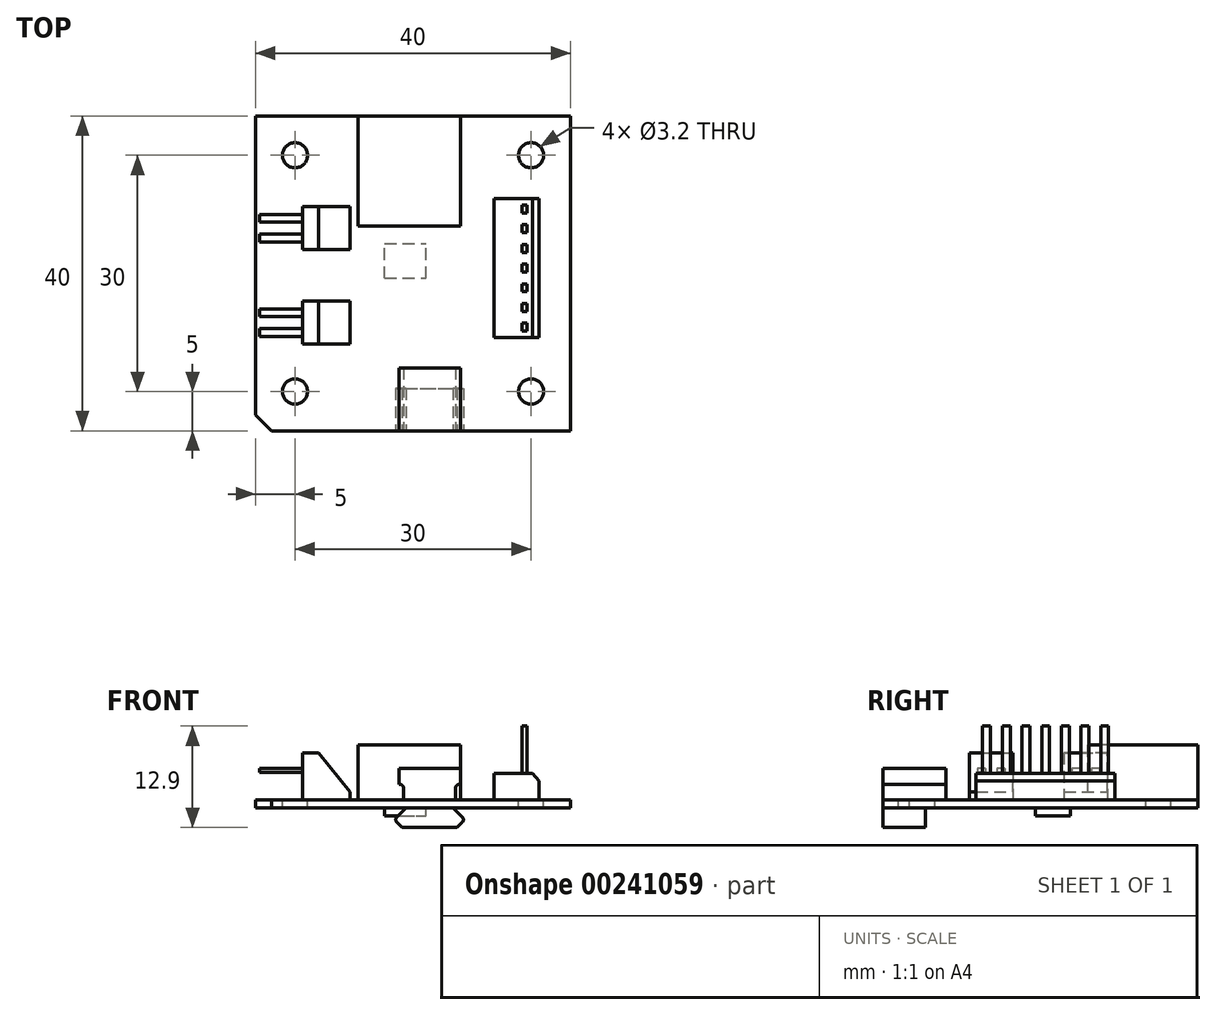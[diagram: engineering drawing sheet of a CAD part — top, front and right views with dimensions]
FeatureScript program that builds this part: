
annotation { "Feature Type Name" : "Feature", "Feature Type Description" : "" }
export const myFeature = defineFeature(function(context is Context, id is Id, definition is map)
    precondition{}
    {
        {
            var Q0;
            Q0=qCreatedBy(makeId("Top.planeOp"),FACE);
            var sketch = newSketch(context, id + "F0", { "sketchPlane" : qUnion([Q0])});
            skLineSegment(sketch, "E0", {"start": v(-20, 20) * mm, "end": v(-20, -18) * mm});
            skLineSegment(sketch, "E1", {"start": v(-18, -20) * mm, "end": v(20, -20) * mm});
            skLineSegment(sketch, "E2", {"start": v(-20, -18) * mm, "end": v(-18, -20) * mm});
            skLineSegment(sketch, "E3", {"start": v(20, 20) * mm, "end": v(20, -20) * mm});
            skLineSegment(sketch, "E4", {"start": v(-20, 20) * mm, "end": v(20, 20) * mm});
            skPoint(sketch, "E5", {"position": v(0, 20) * mm});
            skPoint(sketch, "E6.positionSnap0", {"position": v(20, 0) * mm});
            skSolve(sketch);
        }
        {
            var Q0;
            Q0=makeQuery(id+"F0.imprint","IMPRINT",FACE,{"disambiguationData":[TD([[makeQuery(id+"F0.imprint","IMPRINT",EDGE,{"derivedFrom":sQuery(id+"F0.wireOp",EDGE,"E0")}),1.0]])]});
            extrude(context, id + "F1", {"entities" : qUnion([Q0]), "oppositeDirection" : true, "depth" : 1 * mm});
        }
        {
            var Q0;
            Q0=makeQuery(id+"F1.opExtrude","CAP_FACE",FACE,{"disambiguationData":[OSD([sQuery(id+"F0.wireOp",EDGE,"E0"),sQuery(id+"F0.wireOp",EDGE,"E1"),sQuery(id+"F0.wireOp",EDGE,"wq8KnrCC-K7iv-RLEB-TxgK-UJwxQWP4eZSJ"),sQuery(id+"F0.wireOp",EDGE,"KpYQeONx-miEN-Xjcd-WnpJ-AOX53lkAbQX0"),sQuery(id+"F0.wireOp",EDGE,"kbl2VPpv-Qmzk-IL6K-4Z6z-1lDPvhAcDkAd")])],"isStart":true});
            var sketch = newSketch(context, id + "F2", { "sketchPlane" : qUnion([Q0])});
            skCircle(sketch, "E7", {"center": v(-15, 15) * mm, "radius": 1.6 * mm});
            skCircle(sketch, "E8", {"center": v(-15, -15) * mm, "radius": 1.6 * mm});
            skCircle(sketch, "E9", {"center": v(15, -15) * mm, "radius": 1.6 * mm});
            skCircle(sketch, "E10", {"center": v(15, 15) * mm, "radius": 1.6 * mm});
            skLineSegment(sketch, "E11", {"start": v(-15, 15) * mm, "end": v(15, 15) * mm, "construction": true});
            skLineSegment(sketch, "E12", {"start": v(-15, 15) * mm, "end": v(-15, -15) * mm, "construction": true});
            skPoint(sketch, "E13", {"position": v(0, 15) * mm});
            skPoint(sketch, "E14", {"position": v(-15, 0) * mm});
            skSolve(sketch);
        }
        {
            var Q0;
            Q0 = qSketchRegion(id + "F2", true);
            var Q1;
            Q1=makeQuery(id+"F1.opExtrude","CAP_FACE",FACE,{"disambiguationData":[OSD([sQuery(id+"F0.wireOp",EDGE,"E0"),sQuery(id+"F0.wireOp",EDGE,"E1"),sQuery(id+"F0.wireOp",EDGE,"wq8KnrCC-K7iv-RLEB-TxgK-UJwxQWP4eZSJ"),sQuery(id+"F0.wireOp",EDGE,"KpYQeONx-miEN-Xjcd-WnpJ-AOX53lkAbQX0"),sQuery(id+"F0.wireOp",EDGE,"kbl2VPpv-Qmzk-IL6K-4Z6z-1lDPvhAcDkAd")])],"isStart":false});
            extrude(context, id + "F3", {"entities" : qUnion([Q0]), "operationType" : NewBodyOperationType.REMOVE, "endBound" : BoundingType.UP_TO_SURFACE, "oppositeDirection" : true, "endBoundEntityFace" : qUnion([Q1]), "depth" : 25 * mm});
        }
        {
            var Q0;
            Q0=makeQuery(id+"F1.opExtrude","CAP_FACE",FACE,{"disambiguationData":[OSD([sQuery(id+"F0.wireOp",EDGE,"E0"),sQuery(id+"F0.wireOp",EDGE,"E1"),sQuery(id+"F0.wireOp",EDGE,"wq8KnrCC-K7iv-RLEB-TxgK-UJwxQWP4eZSJ"),sQuery(id+"F0.wireOp",EDGE,"KpYQeONx-miEN-Xjcd-WnpJ-AOX53lkAbQX0"),sQuery(id+"F0.wireOp",EDGE,"kbl2VPpv-Qmzk-IL6K-4Z6z-1lDPvhAcDkAd")])],"isStart":true});
            var sketch = newSketch(context, id + "F4", { "sketchPlane" : qUnion([Q0])});
            skLineSegment(sketch, "E15.bottom", {"start": v(-7, 20) * mm, "end": v(6, 20) * mm});
            skLineSegment(sketch, "E15.top", {"start": v(-7, 6) * mm, "end": v(6, 6) * mm});
            skLineSegment(sketch, "E15.left", {"start": v(-7, 20) * mm, "end": v(-7, 6) * mm});
            skLineSegment(sketch, "E15.right", {"start": v(6, 20) * mm, "end": v(6, 6) * mm});
            skLineSegment(sketch, "E16.0.0", {"start": v(20, -20) * mm, "end": v(20, 20) * mm});
            skLineSegment(sketch, "E16.0.1", {"start": v(20, 20) * mm, "end": v(-20, 20) * mm});
            skLineSegment(sketch, "E16.0.2", {"start": v(-20, 20) * mm, "end": v(-20, -18) * mm});
            skLineSegment(sketch, "E16.0.3", {"start": v(-20, -18) * mm, "end": v(-18, -20) * mm});
            skLineSegment(sketch, "E16.0.4", {"start": v(-18, -20) * mm, "end": v(20, -20) * mm});
            skSolve(sketch);
        }
        {
            var Q0;
            Q0=makeQuery(id+"F4.imprint","IMPRINT",FACE,{"disambiguationData":[TD([[makeQuery(id+"F4.imprint","IMPRINT",EDGE,{"derivedFrom":sQuery(id+"F4.wireOp",EDGE,"E15.top")}),1.0]])]});
            extrude(context, id + "F5", {"entities" : qUnion([Q0]), "depth" : 7 * mm});
        }
        {
            var Q0;
            Q0=makeQuery(id+"F1.opExtrude","SWEPT_FACE",FACE,{"disambiguationData":[OSD([sQuery(id+"F0.wireOp",EDGE,"E1")])]});
            var sketch = newSketch(context, id + "F6", { "sketchPlane" : qUnion([Q0])});
            skLineSegment(sketch, "E17.0.0", {"start": v(-18, 0) * mm, "end": v(-18, 0) * mm});
            skLineSegment(sketch, "E17.0.1", {"start": v(-18, 0) * mm, "end": v(-18, -1) * mm});
            skLineSegment(sketch, "E17.0.2", {"start": v(-18, -1) * mm, "end": v(-18, -1) * mm});
            skLineSegment(sketch, "E17.0.3", {"start": v(-18, 0) * mm, "end": v(-18, -1) * mm});
            skLineSegment(sketch, "E18", {"start": v(-1.2, 0) * mm, "end": v(-1.2, 2) * mm});
            skLineSegment(sketch, "E19", {"start": v(-1.2, 2) * mm, "end": v(-1.8, 2) * mm});
            skLineSegment(sketch, "E20", {"start": v(-1.8, 2) * mm, "end": v(-1.8, 4) * mm});
            skLineSegment(sketch, "E21", {"start": v(-1.8, 4) * mm, "end": v(6, 4) * mm});
            skLineSegment(sketch, "E22", {"start": v(6, 4) * mm, "end": v(6, 2) * mm});
            skLineSegment(sketch, "E23", {"start": v(6, 2) * mm, "end": v(5.4, 2) * mm});
            skLineSegment(sketch, "E24", {"start": v(5.4, 2) * mm, "end": v(5.4, 0) * mm});
            skLineSegment(sketch, "E25", {"start": v(5.4, 0) * mm, "end": v(-1.2, 0) * mm});
            skLineSegment(sketch, "E26.0.0", {"start": v(-7, 0) * mm, "end": v(6, 0) * mm});
            skLineSegment(sketch, "E26.0.1", {"start": v(6, 0) * mm, "end": v(6, 7) * mm});
            skLineSegment(sketch, "E26.0.2", {"start": v(6, 7) * mm, "end": v(-7, 7) * mm});
            skLineSegment(sketch, "E26.0.3", {"start": v(-7, 7) * mm, "end": v(-7, 0) * mm});
            skSolve(sketch);
        }
        {
            var Q0;
            {var subQ1=sQuery(id+"F6.wireOp",EDGE,"E18");Q0=makeQuery(id+"F6.imprint","IMPRINT",FACE,{"disambiguationData":[TD([[makeQuery(id+"F6.imprint","IMPRINT",EDGE,{"derivedFrom":subQ1}),-1.0]])]});}
            extrude(context, id + "F7", {"entities" : qUnion([Q0]), "oppositeDirection" : true, "depth" : 8 * mm});
        }
        {
            var Q0;
            Q0=makeQuery(id+"F7.opExtrude","SWEPT_EDGE",EDGE,{"disambiguationData":[OSD([sQuery(id+"F6.wireOp",EDGE,"E18"),sQuery(id+"F6.wireOp",EDGE,"E19")])]});
            var Q1;
            Q1=makeQuery(id+"F7.opExtrude","SWEPT_EDGE",EDGE,{"disambiguationData":[OSD([sQuery(id+"F6.wireOp",EDGE,"E23"),sQuery(id+"F6.wireOp",EDGE,"E24")])]});
            fillet(context, id + "F8", {"entities" : qUnion([Q0, Q1]), "radius" : 0.5 * mm, "tangentPropagation" : true, "allowEdgeOverflow" : false});
        }
        {
            var Q0;
            Q0=makeQuery(id+"F1.opExtrude","SWEPT_FACE",FACE,{"disambiguationData":[OSD([sQuery(id+"F0.wireOp",EDGE,"E1")])]});
            var sketch = newSketch(context, id + "F9", { "sketchPlane" : qUnion([Q0])});
            skLineSegment(sketch, "E27.0.0", {"start": v(-18, 0) * mm, "end": v(-18, 0) * mm});
            skLineSegment(sketch, "E27.0.1", {"start": v(-18, 0) * mm, "end": v(-18, -1) * mm});
            skLineSegment(sketch, "E27.0.2", {"start": v(-18, -1) * mm, "end": v(-18, -1) * mm});
            skLineSegment(sketch, "E27.0.3", {"start": v(-18, 0) * mm, "end": v(-18, -1) * mm});
            skLineSegment(sketch, "E28.0.0", {"start": v(5.9, 2) * mm, "end": v(6, 2) * mm});
            skLineSegment(sketch, "E28.0.1", {"start": v(6, 2) * mm, "end": v(6, 4) * mm});
            skLineSegment(sketch, "E28.0.2", {"start": v(6, 4) * mm, "end": v(-1.8, 4) * mm});
            skLineSegment(sketch, "E28.0.3", {"start": v(-1.8, 4) * mm, "end": v(-1.8, 2) * mm});
            skLineSegment(sketch, "E28.0.4", {"start": v(-1.8, 2) * mm, "end": v(-1.7, 2) * mm});
            skArc(sketch, "E28.0.5", {"start": v(-1.7, 2) * mm, "mid": v(-1.35, 1.85) * mm, "end": v(-1.2, 1.5) * mm});
            skLineSegment(sketch, "E28.0.6", {"start": v(-1.2, 1.5) * mm, "end": v(-1.2, 0) * mm});
            skLineSegment(sketch, "E28.0.7", {"start": v(-1.2, 0) * mm, "end": v(5.4, 0) * mm});
            skLineSegment(sketch, "E28.0.8", {"start": v(5.4, 0) * mm, "end": v(5.4, 1.5) * mm});
            skArc(sketch, "E28.0.9", {"start": v(5.4, 1.5) * mm, "mid": v(5.55, 1.85) * mm, "end": v(5.9, 2) * mm});
            skLineSegment(sketch, "E29", {"start": v(-0.9, -1) * mm, "end": v(-2.05, -2.15) * mm});
            skLineSegment(sketch, "E30", {"start": v(-2.05, -2.85) * mm, "end": v(-1.4, -3.5) * mm});
            skLineSegment(sketch, "E31", {"start": v(-1.4, -3.5) * mm, "end": v(5.6, -3.5) * mm});
            skLineSegment(sketch, "E32", {"start": v(5.6, -3.5) * mm, "end": v(6.25, -2.85) * mm});
            skLineSegment(sketch, "E33", {"start": v(6.25, -2.15) * mm, "end": v(5.1, -1) * mm});
            skLineSegment(sketch, "E34", {"start": v(5.1, -1) * mm, "end": v(-0.9, -1) * mm});
            skPoint(sketch, "E35", {"position": v(2.1, 4) * mm});
            skPoint(sketch, "E36", {"position": v(2.1, -1) * mm});
            skPoint(sketch, "E37", {"position": v(2.1, -3.5) * mm});
            skPoint(sketch, "E38.visualSharp", {"position": v(-2.4, -2.5) * mm});
            skArc(sketch, "E38.filletArc", {"start": v(-2.05, -2.15) * mm, "mid": v(-2.2, -2.5) * mm, "end": v(-2.05, -2.85) * mm});
            skPoint(sketch, "E39.visualSharp", {"position": v(6.6, -2.5) * mm});
            skArc(sketch, "E39.filletArc", {"start": v(6.25, -2.85) * mm, "mid": v(6.4, -2.5) * mm, "end": v(6.25, -2.15) * mm});
            skSolve(sketch);
        }
        {
            var Q0;
            Q0=makeQuery(id+"F9.imprint","IMPRINT",FACE,{"disambiguationData":[TD([[makeQuery(id+"F9.imprint","IMPRINT",EDGE,{"derivedFrom":sQuery(id+"F9.wireOp",EDGE,"E29")}),1.0]])]});
            extrude(context, id + "F10", {"entities" : qUnion([Q0]), "oppositeDirection" : true, "depth" : 5.4 * mm});
        }
        {
            var Q0;
            Q0=makeQuery(id+"F1.opExtrude","CAP_FACE",FACE,{"disambiguationData":[OSD([sQuery(id+"F0.wireOp",EDGE,"E0"),sQuery(id+"F0.wireOp",EDGE,"E1"),sQuery(id+"F0.wireOp",EDGE,"E2"),sQuery(id+"F0.wireOp",EDGE,"E3"),sQuery(id+"F0.wireOp",EDGE,"E4")])],"isStart":false});
            var sketch = newSketch(context, id + "F11", { "sketchPlane" : qUnion([Q0])});
            skLineSegment(sketch, "E40.bottom", {"start": v(-3.6, 0.6) * mm, "end": v(1.65, 0.6) * mm});
            skLineSegment(sketch, "E40.top", {"start": v(-3.6, -3.8) * mm, "end": v(1.65, -3.8) * mm});
            skLineSegment(sketch, "E40.left", {"start": v(-3.6, 0.6) * mm, "end": v(-3.6, -3.8) * mm});
            skLineSegment(sketch, "E40.right", {"start": v(1.65, 0.6) * mm, "end": v(1.65, -3.8) * mm});
            skSolve(sketch);
        }
        {
            var Q0;
            Q0=makeQuery(id+"F11.imprint","IMPRINT",FACE,{"disambiguationData":[TD([[makeQuery(id+"F11.imprint","IMPRINT",EDGE,{"derivedFrom":sQuery(id+"F11.wireOp",EDGE,"E40.bottom")}),-1.0]])]});
            extrude(context, id + "F12", {"entities" : qUnion([Q0]), "depth" : 1 * mm});
        }
        {
            var Q0;
            Q0=makeQuery(id+"F1.opExtrude","CAP_FACE",FACE,{"disambiguationData":[OSD([sQuery(id+"F0.wireOp",EDGE,"E0"),sQuery(id+"F0.wireOp",EDGE,"E1"),sQuery(id+"F0.wireOp",EDGE,"E2"),sQuery(id+"F0.wireOp",EDGE,"E3"),sQuery(id+"F0.wireOp",EDGE,"E4")])],"isStart":true});
            var sketch = newSketch(context, id + "F13", { "sketchPlane" : qUnion([Q0])});
            skLineSegment(sketch, "E41.bottom", {"start": v(10.3, 9.5) * mm, "end": v(16, 9.5) * mm});
            skLineSegment(sketch, "E41.top", {"start": v(10.3, -8.15) * mm, "end": v(16, -8.15) * mm});
            skLineSegment(sketch, "E41.left", {"start": v(10.3, 9.5) * mm, "end": v(10.3, -8.15) * mm});
            skLineSegment(sketch, "E41.right", {"start": v(16, 9.5) * mm, "end": v(16, -8.15) * mm});
            skSolve(sketch);
        }
        {
            var Q0;
            Q0=makeQuery(id+"F13.imprint","IMPRINT",FACE,{"disambiguationData":[TD([[makeQuery(id+"F13.imprint","IMPRINT",EDGE,{"derivedFrom":sQuery(id+"F13.wireOp",EDGE,"E41.bottom")}),-1.0]])]});
            extrude(context, id + "F14", {"entities" : qUnion([Q0]), "depth" : 3.4 * mm});
        }
        {
            var Q0;
            Q0=makeQuery(id+"F14.opExtrude","CAP_FACE",FACE,{"disambiguationData":[OSD([sQuery(id+"F13.wireOp",EDGE,"E41.bottom"),sQuery(id+"F13.wireOp",EDGE,"E41.top"),sQuery(id+"F13.wireOp",EDGE,"E41.left"),sQuery(id+"F13.wireOp",EDGE,"E41.right")])],"isStart":false});
            var sketch = newSketch(context, id + "F15", { "sketchPlane" : qUnion([Q0])});
            skLineSegment(sketch, "E42.bottom", {"start": v(13.85, 8.67) * mm, "end": v(14.5, 8.67) * mm});
            skLineSegment(sketch, "E42.top", {"start": v(13.85, 7.67) * mm, "end": v(14.5, 7.67) * mm});
            skLineSegment(sketch, "E42.left", {"start": v(13.85, 8.67) * mm, "end": v(13.85, 7.67) * mm});
            skLineSegment(sketch, "E42.right", {"start": v(14.5, 8.67) * mm, "end": v(14.5, 7.67) * mm});
            skLineSegment(sketch, "E43.bottom", {"start": v(13.85, 6.17) * mm, "end": v(14.5, 6.17) * mm});
            skLineSegment(sketch, "E43.top", {"start": v(13.85, 5.17) * mm, "end": v(14.5, 5.17) * mm});
            skLineSegment(sketch, "E43.left", {"start": v(13.85, 6.17) * mm, "end": v(13.85, 5.17) * mm});
            skLineSegment(sketch, "E43.right", {"start": v(14.5, 6.17) * mm, "end": v(14.5, 5.17) * mm});
            skLineSegment(sketch, "E44.bottom", {"start": v(13.85, 3.67) * mm, "end": v(14.5, 3.67) * mm});
            skLineSegment(sketch, "E44.top", {"start": v(13.85, 2.67) * mm, "end": v(14.5, 2.67) * mm});
            skLineSegment(sketch, "E44.left", {"start": v(13.85, 3.67) * mm, "end": v(13.85, 2.67) * mm});
            skLineSegment(sketch, "E44.right", {"start": v(14.5, 3.67) * mm, "end": v(14.5, 2.67) * mm});
            skLineSegment(sketch, "E45.bottom", {"start": v(13.85, 1.17) * mm, "end": v(14.5, 1.17) * mm});
            skLineSegment(sketch, "E45.top", {"start": v(13.85, 0.17) * mm, "end": v(14.5, 0.17) * mm});
            skLineSegment(sketch, "E45.left", {"start": v(13.85, 1.17) * mm, "end": v(13.85, 0.17) * mm});
            skLineSegment(sketch, "E45.right", {"start": v(14.5, 1.17) * mm, "end": v(14.5, 0.17) * mm});
            skLineSegment(sketch, "E46.bottom", {"start": v(14.5, -1.33) * mm, "end": v(13.85, -1.33) * mm});
            skLineSegment(sketch, "E46.top", {"start": v(14.5, -2.33) * mm, "end": v(13.85, -2.33) * mm});
            skLineSegment(sketch, "E46.left", {"start": v(14.5, -1.33) * mm, "end": v(14.5, -2.33) * mm});
            skLineSegment(sketch, "E46.right", {"start": v(13.85, -1.33) * mm, "end": v(13.85, -2.33) * mm});
            skLineSegment(sketch, "E47.bottom", {"start": v(14.5, -3.83) * mm, "end": v(13.85, -3.83) * mm});
            skLineSegment(sketch, "E47.top", {"start": v(14.5, -4.83) * mm, "end": v(13.85, -4.83) * mm});
            skLineSegment(sketch, "E47.left", {"start": v(14.5, -3.83) * mm, "end": v(14.5, -4.83) * mm});
            skLineSegment(sketch, "E47.right", {"start": v(13.85, -3.83) * mm, "end": v(13.85, -4.83) * mm});
            skLineSegment(sketch, "E48.bottom", {"start": v(14.5, -6.33) * mm, "end": v(13.85, -6.33) * mm});
            skLineSegment(sketch, "E48.top", {"start": v(14.5, -7.33) * mm, "end": v(13.85, -7.33) * mm});
            skLineSegment(sketch, "E48.left", {"start": v(14.5, -6.33) * mm, "end": v(14.5, -7.33) * mm});
            skLineSegment(sketch, "E48.right", {"start": v(13.85, -6.33) * mm, "end": v(13.85, -7.33) * mm});
            skLineSegment(sketch, "E49", {"start": v(14.5, 8.67) * mm, "end": v(14.5, 6.17) * mm, "construction": true});
            skLineSegment(sketch, "E50", {"start": v(14.5, 6.17) * mm, "end": v(14.5, 3.67) * mm, "construction": true});
            skLineSegment(sketch, "E51", {"start": v(14.5, 3.67) * mm, "end": v(14.5, 1.17) * mm, "construction": true});
            skLineSegment(sketch, "E52", {"start": v(14.5, 1.17) * mm, "end": v(14.5, -1.33) * mm, "construction": true});
            skLineSegment(sketch, "E53", {"start": v(14.5, -1.33) * mm, "end": v(14.5, -3.83) * mm, "construction": true});
            skLineSegment(sketch, "E54", {"start": v(14.5, -3.83) * mm, "end": v(14.5, -6.33) * mm, "construction": true});
            skLineSegment(sketch, "E55", {"start": v(13.85, 8.67) * mm, "end": v(13.85, -7.33) * mm, "construction": true});
            skPoint(sketch, "E56", {"position": v(13.85, 0.67) * mm});
            skPoint(sketch, "E57", {"position": v(10.3, 0.67) * mm});
            skSolve(sketch);
        }
        {
            var Q0;
            Q0=makeQuery(id+"F15.imprint","IMPRINT",FACE,{"disambiguationData":[TD([[makeQuery(id+"F15.imprint","IMPRINT",EDGE,{"derivedFrom":sQuery(id+"F15.wireOp",EDGE,"E42.bottom")}),-1.0]])]});
            var Q1;
            Q1=makeQuery(id+"F15.imprint","IMPRINT",FACE,{"disambiguationData":[TD([[makeQuery(id+"F15.imprint","IMPRINT",EDGE,{"derivedFrom":sQuery(id+"F15.wireOp",EDGE,"E43.bottom")}),-1.0]])]});
            var Q2;
            Q2=makeQuery(id+"F15.imprint","IMPRINT",FACE,{"disambiguationData":[TD([[makeQuery(id+"F15.imprint","IMPRINT",EDGE,{"derivedFrom":sQuery(id+"F15.wireOp",EDGE,"E44.bottom")}),-1.0]])]});
            var Q3;
            Q3=makeQuery(id+"F15.imprint","IMPRINT",FACE,{"disambiguationData":[TD([[makeQuery(id+"F15.imprint","IMPRINT",EDGE,{"derivedFrom":sQuery(id+"F15.wireOp",EDGE,"E45.bottom")}),-1.0]])]});
            var Q4;
            Q4=makeQuery(id+"F15.imprint","IMPRINT",FACE,{"disambiguationData":[TD([[makeQuery(id+"F15.imprint","IMPRINT",EDGE,{"derivedFrom":sQuery(id+"F15.wireOp",EDGE,"E46.bottom")}),1.0]])]});
            var Q5;
            Q5=makeQuery(id+"F15.imprint","IMPRINT",FACE,{"disambiguationData":[TD([[makeQuery(id+"F15.imprint","IMPRINT",EDGE,{"derivedFrom":sQuery(id+"F15.wireOp",EDGE,"E47.bottom")}),1.0]])]});
            var Q6;
            Q6=makeQuery(id+"F15.imprint","IMPRINT",FACE,{"disambiguationData":[TD([[makeQuery(id+"F15.imprint","IMPRINT",EDGE,{"derivedFrom":sQuery(id+"F15.wireOp",EDGE,"E48.bottom")}),1.0]])]});
            extrude(context, id + "F16", {"entities" : qUnion([Q0, Q1, Q2, Q3, Q4, Q5, Q6]), "operationType" : NewBodyOperationType.ADD, "depth" : 6 * mm});
        }
        {
            var Q0;
            Q0=makeQuery(id+"F14.opExtrude","SWEPT_FACE",FACE,{"disambiguationData":[OSD([sQuery(id+"F13.wireOp",EDGE,"E41.top")])]});
            var sketch = newSketch(context, id + "F17", { "sketchPlane" : qUnion([Q0])});
            skLineSegment(sketch, "E58", {"start": v(15.2, 3.4) * mm, "end": v(16, 2.4) * mm});
            skLineSegment(sketch, "E59", {"start": v(16, 2.4) * mm, "end": v(16, 3.4) * mm});
            skLineSegment(sketch, "E60", {"start": v(16, 3.4) * mm, "end": v(15.2, 3.4) * mm});
            skLineSegment(sketch, "E61", {"start": v(16, 1.9) * mm, "end": v(15.2, 1.4) * mm});
            skLineSegment(sketch, "E62", {"start": v(15.2, 1.4) * mm, "end": v(15.2, 0) * mm});
            skLineSegment(sketch, "E63", {"start": v(15.2, 0) * mm, "end": v(16, 0) * mm});
            skLineSegment(sketch, "E64", {"start": v(16, 0) * mm, "end": v(16, 1.9) * mm});
            skSolve(sketch);
        }
        {
            var Q0;
            Q0=makeQuery(id+"F17.imprint","IMPRINT",FACE,{"disambiguationData":[TD([[makeQuery(id+"F17.imprint","IMPRINT",EDGE,{"derivedFrom":sQuery(id+"F17.wireOp",EDGE,"E58")}),1.0]])]});
            extrude(context, id + "F18", {"entities" : qUnion([Q0]), "operationType" : NewBodyOperationType.REMOVE, "endBound" : BoundingType.UP_TO_NEXT, "oppositeDirection" : true, "depth" : 25 * mm});
        }
        {
            var Q0;
            Q0=makeQuery(id+"F1.opExtrude","CAP_FACE",FACE,{"disambiguationData":[OSD([sQuery(id+"F0.wireOp",EDGE,"E0"),sQuery(id+"F0.wireOp",EDGE,"E1"),sQuery(id+"F0.wireOp",EDGE,"E2"),sQuery(id+"F0.wireOp",EDGE,"E3"),sQuery(id+"F0.wireOp",EDGE,"E4")])],"isStart":true});
            var sketch = newSketch(context, id + "F19", { "sketchPlane" : qUnion([Q0])});
            skLineSegment(sketch, "E65.bottom", {"start": v(-14, -4) * mm, "end": v(-8, -4) * mm});
            skLineSegment(sketch, "E65.top", {"start": v(-14, -9.5) * mm, "end": v(-8, -9.5) * mm});
            skLineSegment(sketch, "E65.left", {"start": v(-14, -4) * mm, "end": v(-14, -9.5) * mm});
            skLineSegment(sketch, "E65.right", {"start": v(-8, -4) * mm, "end": v(-8, -9.5) * mm});
            skLineSegment(sketch, "E66.bottom", {"start": v(-14, 8.5) * mm, "end": v(-8, 8.5) * mm});
            skLineSegment(sketch, "E66.top", {"start": v(-14, 3) * mm, "end": v(-8, 3) * mm});
            skLineSegment(sketch, "E66.left", {"start": v(-14, 8.5) * mm, "end": v(-14, 3) * mm});
            skLineSegment(sketch, "E66.right", {"start": v(-8, 8.5) * mm, "end": v(-8, 3) * mm});
            skSolve(sketch);
        }
        {
            var Q0;
            Q0=makeQuery(id+"F19.imprint","IMPRINT",FACE,{"disambiguationData":[TD([[makeQuery(id+"F19.imprint","IMPRINT",EDGE,{"derivedFrom":sQuery(id+"F19.wireOp",EDGE,"E66.bottom")}),-1.0]])]});
            var Q1;
            Q1=makeQuery(id+"F19.imprint","IMPRINT",FACE,{"disambiguationData":[TD([[makeQuery(id+"F19.imprint","IMPRINT",EDGE,{"derivedFrom":sQuery(id+"F19.wireOp",EDGE,"E65.bottom")}),-1.0]])]});
            extrude(context, id + "F20", {"entities" : qUnion([Q0, Q1]), "depth" : 6 * mm});
        }
        {
            var Q0;
            Q0=makeQuery(id+"F20.opExtrude","SWEPT_FACE",FACE,{"disambiguationData":[OSD([sQuery(id+"F19.wireOp",EDGE,"E66.left")])]});
            var sketch = newSketch(context, id + "F21", { "sketchPlane" : qUnion([Q0])});
            skLineSegment(sketch, "E67.bottom", {"start": v(-7.5, 4) * mm, "end": v(-6.5, 4) * mm});
            skLineSegment(sketch, "E67.top", {"start": v(-7.5, 3.5) * mm, "end": v(-6.5, 3.5) * mm});
            skLineSegment(sketch, "E67.left", {"start": v(-7.5, 4) * mm, "end": v(-7.5, 3.5) * mm});
            skLineSegment(sketch, "E67.right", {"start": v(-6.5, 4) * mm, "end": v(-6.5, 3.5) * mm});
            skLineSegment(sketch, "E68.bottom", {"start": v(-5, 4) * mm, "end": v(-4, 4) * mm});
            skLineSegment(sketch, "E68.top", {"start": v(-5, 3.5) * mm, "end": v(-4, 3.5) * mm});
            skLineSegment(sketch, "E68.left", {"start": v(-5, 4) * mm, "end": v(-5, 3.5) * mm});
            skLineSegment(sketch, "E68.right", {"start": v(-4, 4) * mm, "end": v(-4, 3.5) * mm});
            skLineSegment(sketch, "E69", {"start": v(-6.5, 3.75) * mm, "end": v(-5, 3.75) * mm, "construction": true});
            skPoint(sketch, "E70", {"position": v(-5.75, 6) * mm});
            skPoint(sketch, "E71", {"position": v(-5.75, 3.75) * mm});
            skSolve(sketch);
        }
        {
            var Q0;
            Q0=makeQuery(id+"F21.imprint","IMPRINT",FACE,{"disambiguationData":[TD([[makeQuery(id+"F21.imprint","IMPRINT",EDGE,{"derivedFrom":sQuery(id+"F21.wireOp",EDGE,"E67.bottom")}),-1.0]])]});
            var Q1;
            Q1=makeQuery(id+"F21.imprint","IMPRINT",FACE,{"disambiguationData":[TD([[makeQuery(id+"F21.imprint","IMPRINT",EDGE,{"derivedFrom":sQuery(id+"F21.wireOp",EDGE,"E68.bottom")}),-1.0]])]});
            extrude(context, id + "F22", {"entities" : qUnion([Q0, Q1]), "operationType" : NewBodyOperationType.ADD, "depth" : 5.5 * mm});
        }
        {
            var Q0;
            Q0=makeQuery(id+"F20.opExtrude","SWEPT_FACE",FACE,{"disambiguationData":[OSD([sQuery(id+"F19.wireOp",EDGE,"E66.bottom")])]});
            var sketch = newSketch(context, id + "F23", { "sketchPlane" : qUnion([Q0])});
            skLineSegment(sketch, "E72", {"start": v(8, 6) * mm, "end": v(8, 1) * mm});
            skLineSegment(sketch, "E73", {"start": v(8, 1) * mm, "end": v(12, 6) * mm});
            skLineSegment(sketch, "E74", {"start": v(12, 6) * mm, "end": v(8, 6) * mm});
            skSolve(sketch);
        }
        {
            var Q0;
            Q0=makeQuery(id+"F23.imprint","IMPRINT",FACE,{"disambiguationData":[TD([[makeQuery(id+"F23.imprint","IMPRINT",EDGE,{"derivedFrom":sQuery(id+"F23.wireOp",EDGE,"E72")}),1.0]])]});
            extrude(context, id + "F24", {"entities" : qUnion([Q0]), "operationType" : NewBodyOperationType.REMOVE, "endBound" : BoundingType.UP_TO_NEXT, "oppositeDirection" : true, "depth" : 25 * mm});
        }
        {
            var Q0;
            Q0=makeQuery(id+"F20.opExtrude","SWEPT_BODY",BODY,{"disambiguationData":[OSD([sQuery(id+"F19.wireOp",EDGE,"E65.bottom"),sQuery(id+"F19.wireOp",EDGE,"E65.top"),sQuery(id+"F19.wireOp",EDGE,"E65.left"),sQuery(id+"F19.wireOp",EDGE,"E65.right")])]});
            deleteBodies(context, id + "F25", {"entities" : qUnion([Q0])});
        }
        {
            var Q0;
            Q0=makeQuery(id+"F20.opExtrude","SWEPT_BODY",BODY,{"disambiguationData":[OSD([sQuery(id+"F19.wireOp",EDGE,"E66.bottom"),sQuery(id+"F19.wireOp",EDGE,"E66.top"),sQuery(id+"F19.wireOp",EDGE,"E66.left"),sQuery(id+"F19.wireOp",EDGE,"E66.right")])]});
            transform(context, id + "F26", {"entities" : qUnion([Q0]), "transformType" : TransformType.TRANSLATION_3D, "dx" : 0 * mm, "dy" : 0 * mm, "dz" : 12 * mm, "makeCopy" : true});
        }
        {
            var Q0;
            Q0=makeQuery(id+"F26.opPattern","COPY",BODY,{"derivedFrom":makeQuery(id+"F20.opExtrude","SWEPT_BODY",BODY,{"disambiguationData":[OSD([sQuery(id+"F19.wireOp",EDGE,"E66.bottom"),sQuery(id+"F19.wireOp",EDGE,"E66.top"),sQuery(id+"F19.wireOp",EDGE,"E66.left"),sQuery(id+"F19.wireOp",EDGE,"E66.right")])]}),"instanceName":"1"});
            deleteBodies(context, id + "F27", {"entities" : qUnion([Q0])});
        }
        {
            var Q0;
            Q0=makeQuery(id+"F20.opExtrude","SWEPT_BODY",BODY,{"disambiguationData":[OSD([sQuery(id+"F19.wireOp",EDGE,"E66.bottom"),sQuery(id+"F19.wireOp",EDGE,"E66.top"),sQuery(id+"F19.wireOp",EDGE,"E66.left"),sQuery(id+"F19.wireOp",EDGE,"E66.right")])]});
            transform(context, id + "F28", {"entities" : qUnion([Q0]), "transformType" : TransformType.TRANSLATION_3D, "dx" : 0 * mm, "dy" : -12 * mm, "dz" : 0 * mm, "makeCopy" : true});
        }
    });
